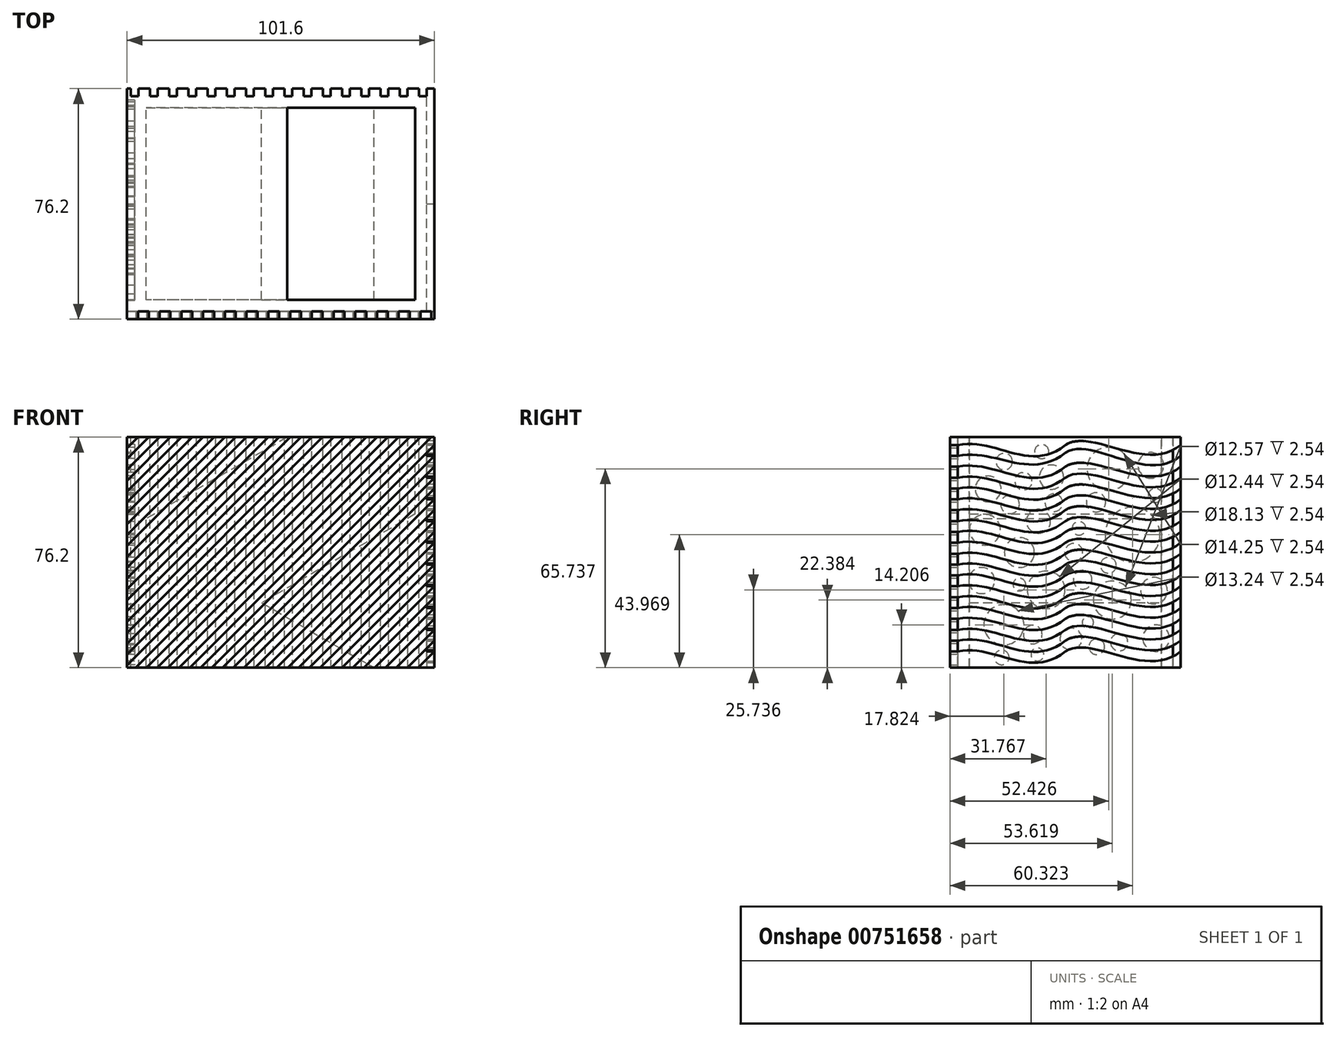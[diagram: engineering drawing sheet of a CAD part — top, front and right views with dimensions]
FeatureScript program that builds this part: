
annotation { "Feature Type Name" : "Feature", "Feature Type Description" : "" }
export const myFeature = defineFeature(function(context is Context, id is Id, definition is map)
    precondition{}
    {
        {
            var Q0;
            Q0=qCreatedBy(makeId("Front.planeOp"),FACE);
            var sketch = newSketch(context, id + "F0", { "sketchPlane" : qUnion([Q0])});
            skLineSegment(sketch, "E0.bottom", {"start": v(50.8, 38.1) * mm, "end": v(-50.8, 38.1) * mm});
            skLineSegment(sketch, "E0.top", {"start": v(50.8, -38.1) * mm, "end": v(-50.8, -38.1) * mm});
            skLineSegment(sketch, "E0.left", {"start": v(50.8, 38.1) * mm, "end": v(50.8, -38.1) * mm});
            skLineSegment(sketch, "E0.right", {"start": v(-50.8, 38.1) * mm, "end": v(-50.8, -38.1) * mm});
            skPoint(sketch, "E0.middle", {"position": v(0, 0) * mm});
            skLineSegment(sketch, "E1", {"start": v(44.45, -38.1) * mm, "end": v(44.45, 38.1) * mm});
            skLineSegment(sketch, "E2.MirrorCS", {"start": v(-44.45, -38.1) * mm, "end": v(-44.45, 38.1) * mm});
            skLineSegment(sketch, "E3", {"start": v(44.45, 12.7) * mm, "end": v(-6.35, -16.63) * mm});
            skLineSegment(sketch, "E4", {"start": v(-6.35, -16.63) * mm, "end": v(30.84, -38.1) * mm});
            skLineSegment(sketch, "E5", {"start": v(2.16, 38.1) * mm, "end": v(-44.45, 11.2) * mm});
            skSolve(sketch);
        }
        {
            var Q0;
            {var subQ0=sQuery(id+"F0.wireOp",EDGE,"E0.left");Q0=makeQuery(id+"F0.imprint","IMPRINT",FACE,{"disambiguationData":[TD([[makeQuery(id+"F0.imprint","IMPRINT",EDGE,{"derivedFrom":subQ0}),-1.0]])]});}
            var Q1;
            {var subQ0=sQuery(id+"F0.wireOp",EDGE,"E0.right");Q1=makeQuery(id+"F0.imprint","IMPRINT",FACE,{"disambiguationData":[TD([[makeQuery(id+"F0.imprint","IMPRINT",EDGE,{"derivedFrom":subQ0}),1.0]])]});}
            var Q2;
            {var subQ4=sQuery(id+"F0.wireOp",EDGE,"E3");Q2=makeQuery(id+"F0.imprint","IMPRINT",FACE,{"disambiguationData":[TD([[makeQuery(id+"F0.imprint","IMPRINT",EDGE,{"derivedFrom":subQ4}),1.0]])]});}
            var Q3;
            {var subQ3=sQuery(id+"F0.wireOp",EDGE,"E5");Q3=makeQuery(id+"F0.imprint","IMPRINT",FACE,{"disambiguationData":[TD([[makeQuery(id+"F0.imprint","IMPRINT",EDGE,{"derivedFrom":subQ3}),-1.0]])]});}
            extrude(context, id + "F1", {"entities" : qUnion([Q0, Q1, Q2, Q3]), "endBound" : BoundingType.SYMMETRIC, "depth" : 76.2 * mm, "offsetDistance" : 25.4 * mm});
        }
        {
            var Q0;
            Q0=makeQuery(id+"F1.opExtrude","CAP_FACE",FACE,{"disambiguationData":[OSD([sQuery(id+"F0.wireOp",EDGE,"E0.bottom"),sQuery(id+"F0.wireOp",EDGE,"E0.top"),sQuery(id+"F0.wireOp",EDGE,"E0.left"),sQuery(id+"F0.wireOp",EDGE,"E1"),sQuery(id+"F0.wireOp",EDGE,"E3"),sQuery(id+"F0.wireOp",EDGE,"E4")])],"isStart":true});
            var sketch = newSketch(context, id + "F2", { "sketchPlane" : qUnion([Q0])});
            skLineSegment(sketch, "E6.bottom", {"start": v(-50.8, 38.1) * mm, "end": v(50.8, 38.1) * mm});
            skLineSegment(sketch, "E6.top", {"start": v(-50.8, -38.1) * mm, "end": v(50.8, -38.1) * mm});
            skLineSegment(sketch, "E6.left", {"start": v(-50.8, 38.1) * mm, "end": v(-50.8, -38.1) * mm});
            skLineSegment(sketch, "E6.right", {"start": v(50.8, 38.1) * mm, "end": v(50.8, -38.1) * mm});
            skPoint(sketch, "E6.middle", {"position": v(0, 0) * mm});
            skSolve(sketch);
        }
        {
            var Q0;
            Q0 = qSketchRegion(id + "F2", true);
            extrude(context, id + "F3", {"entities" : qUnion([Q0]), "operationType" : NewBodyOperationType.ADD, "oppositeDirection" : true, "depth" : 6.35 * mm, "offsetDistance" : 25.4 * mm});
        }
        {
            var Q0;
            Q0=makeQuery(id+"F1.opExtrude","CAP_FACE",FACE,{"disambiguationData":[OSD([sQuery(id+"F0.wireOp",EDGE,"E0.bottom"),sQuery(id+"F0.wireOp",EDGE,"E0.top"),sQuery(id+"F0.wireOp",EDGE,"E0.right"),sQuery(id+"F0.wireOp",EDGE,"E2.MirrorCS"),sQuery(id+"F0.wireOp",EDGE,"E5")])],"isStart":false});
            var sketch = newSketch(context, id + "F4", { "sketchPlane" : qUnion([Q0])});
            skLineSegment(sketch, "E7.bottom", {"start": v(-50.8, 38.1) * mm, "end": v(50.8, 38.1) * mm});
            skLineSegment(sketch, "E7.top", {"start": v(-50.8, -38.1) * mm, "end": v(50.8, -38.1) * mm});
            skLineSegment(sketch, "E7.left", {"start": v(-50.8, 38.1) * mm, "end": v(-50.8, -38.1) * mm});
            skLineSegment(sketch, "E7.right", {"start": v(50.8, 38.1) * mm, "end": v(50.8, -38.1) * mm});
            skPoint(sketch, "E7.middle", {"position": v(0, 0) * mm});
            skSolve(sketch);
        }
        {
            var Q0;
            Q0 = qSketchRegion(id + "F4", true);
            extrude(context, id + "F5", {"entities" : qUnion([Q0]), "operationType" : NewBodyOperationType.ADD, "oppositeDirection" : true, "depth" : 6.35 * mm, "offsetDistance" : 25.4 * mm});
        }
        {
            var Q0;
            {var subQ0=sQuery(id+"F0.wireOp",EDGE,"E0.top");var subQ1=sQuery(id+"F0.wireOp",EDGE,"E0.bottom");Q0=makeQuery(id+"F5.boolean.opBoolean","MERGE",FACE,{"derivedFrom":[makeQuery(id+"F1.opExtrude","CAP_FACE",FACE,{"disambiguationData":[OSD([subQ1,subQ0,sQuery(id+"F0.wireOp",EDGE,"E0.left"),sQuery(id+"F0.wireOp",EDGE,"E1"),sQuery(id+"F0.wireOp",EDGE,"E3"),sQuery(id+"F0.wireOp",EDGE,"E4")])],"isStart":false}),makeQuery(id+"F1.opExtrude","CAP_FACE",FACE,{"disambiguationData":[OSD([subQ1,subQ0,sQuery(id+"F0.wireOp",EDGE,"E0.right"),sQuery(id+"F0.wireOp",EDGE,"E2.MirrorCS"),sQuery(id+"F0.wireOp",EDGE,"E5")])],"isStart":false}),makeQuery(id+"F5.opExtrude","CAP_FACE",FACE,{"disambiguationData":[OSD([sQuery(id+"F4.wireOp",EDGE,"E7.bottom"),sQuery(id+"F4.wireOp",EDGE,"E7.top"),sQuery(id+"F4.wireOp",EDGE,"E7.left"),sQuery(id+"F4.wireOp",EDGE,"E7.right")])],"isStart":true})]});}
            var sketch = newSketch(context, id + "F6", { "sketchPlane" : qUnion([Q0])});
            skLineSegment(sketch, "E8", {"start": v(-50.8, 34.5) * mm, "end": v(-47.2, 38.1) * mm});
            skLineSegment(sketch, "E9", {"start": v(-50.8, 30.92) * mm, "end": v(-43.62, 38.1) * mm});
            skLineSegment(sketch, "E10", {"start": v(-50.8, 27.32) * mm, "end": v(-40.02, 38.1) * mm});
            skLineSegment(sketch, "E11", {"start": v(-50.8, 23.73) * mm, "end": v(-36.43, 38.1) * mm});
            skLineSegment(sketch, "E12", {"start": v(-50.8, 20.14) * mm, "end": v(-32.84, 38.1) * mm});
            skLineSegment(sketch, "E13", {"start": v(-50.8, 16.55) * mm, "end": v(-29.25, 38.1) * mm});
            skLineSegment(sketch, "E14", {"start": v(-50.8, 12.96) * mm, "end": v(-25.66, 38.1) * mm});
            skLineSegment(sketch, "E15", {"start": v(-50.8, 9.36) * mm, "end": v(-22.06, 38.1) * mm});
            skLineSegment(sketch, "E16", {"start": v(-50.8, 5.77) * mm, "end": v(-18.47, 38.1) * mm});
            skLineSegment(sketch, "E17", {"start": v(-50.8, 2.18) * mm, "end": v(-14.88, 38.1) * mm});
            skLineSegment(sketch, "E18", {"start": v(-50.8, -1.41) * mm, "end": v(-11.29, 38.1) * mm});
            skLineSegment(sketch, "E19", {"start": v(-50.8, -5) * mm, "end": v(-7.7, 38.1) * mm});
            skLineSegment(sketch, "E20", {"start": v(-4.1, 38.1) * mm, "end": v(-50.8, -8.6) * mm});
            skLineSegment(sketch, "E21", {"start": v(-50.8, -12.19) * mm, "end": v(-0.51, 38.1) * mm});
            skLineSegment(sketch, "E22", {"start": v(-50.8, -15.78) * mm, "end": v(3.08, 38.1) * mm});
            skLineSegment(sketch, "E23", {"start": v(6.67, 38.1) * mm, "end": v(-50.8, -19.37) * mm});
            skLineSegment(sketch, "E24", {"start": v(-50.8, -22.97) * mm, "end": v(10.27, 38.1) * mm});
            skLineSegment(sketch, "E25", {"start": v(13.86, 38.1) * mm, "end": v(-50.8, -26.56) * mm});
            skLineSegment(sketch, "E26", {"start": v(-50.8, -30.15) * mm, "end": v(17.45, 38.1) * mm});
            skLineSegment(sketch, "E27", {"start": v(-50.8, -33.74) * mm, "end": v(21.04, 38.1) * mm});
            skLineSegment(sketch, "E28", {"start": v(-50.8, -37.33) * mm, "end": v(24.63, 38.1) * mm});
            skLineSegment(sketch, "E29", {"start": v(-47.97, -38.1) * mm, "end": v(28.23, 38.1) * mm});
            skLineSegment(sketch, "E30", {"start": v(-44.38, -38.1) * mm, "end": v(31.82, 38.1) * mm});
            skLineSegment(sketch, "E31", {"start": v(35.41, 38.1) * mm, "end": v(-40.79, -38.1) * mm});
            skLineSegment(sketch, "E32", {"start": v(-37.2, -38.1) * mm, "end": v(39, 38.1) * mm});
            skLineSegment(sketch, "E33", {"start": v(42.6, 38.1) * mm, "end": v(-33.6, -38.1) * mm});
            skLineSegment(sketch, "E34", {"start": v(-30.01, -38.1) * mm, "end": v(46.19, 38.1) * mm});
            skLineSegment(sketch, "E35", {"start": v(49.78, 38.1) * mm, "end": v(-26.42, -38.1) * mm});
            skLineSegment(sketch, "E36", {"start": v(50.8, 35.53) * mm, "end": v(-22.83, -38.1) * mm});
            skLineSegment(sketch, "E37", {"start": v(-19.24, -38.1) * mm, "end": v(50.8, 31.94) * mm});
            skLineSegment(sketch, "E38", {"start": v(50.8, 28.34) * mm, "end": v(-15.64, -38.1) * mm});
            skLineSegment(sketch, "E39", {"start": v(-12.05, -38.1) * mm, "end": v(50.8, 24.75) * mm});
            skLineSegment(sketch, "E40", {"start": v(50.8, 21.16) * mm, "end": v(-8.46, -38.1) * mm});
            skLineSegment(sketch, "E41", {"start": v(-4.87, -38.1) * mm, "end": v(50.8, 17.57) * mm});
            skLineSegment(sketch, "E42", {"start": v(50.8, 13.98) * mm, "end": v(-1.28, -38.1) * mm});
            skLineSegment(sketch, "E43", {"start": v(2.32, -38.1) * mm, "end": v(50.8, 10.38) * mm});
            skLineSegment(sketch, "E44", {"start": v(50.8, 6.8) * mm, "end": v(5.9, -38.1) * mm});
            skLineSegment(sketch, "E45", {"start": v(9.5, -38.1) * mm, "end": v(50.8, 3.2) * mm});
            skLineSegment(sketch, "E46", {"start": v(50.8, -0.4) * mm, "end": v(13.1, -38.1) * mm});
            skLineSegment(sketch, "E47", {"start": v(16.68, -38.1) * mm, "end": v(50.8, -3.98) * mm});
            skLineSegment(sketch, "E48", {"start": v(50.8, -7.58) * mm, "end": v(20.28, -38.1) * mm});
            skLineSegment(sketch, "E49", {"start": v(23.87, -38.1) * mm, "end": v(50.8, -11.17) * mm});
            skLineSegment(sketch, "E50", {"start": v(50.8, -14.76) * mm, "end": v(27.46, -38.1) * mm});
            skLineSegment(sketch, "E51", {"start": v(31.05, -38.1) * mm, "end": v(50.8, -18.35) * mm});
            skLineSegment(sketch, "E52", {"start": v(34.64, -38.1) * mm, "end": v(50.8, -21.94) * mm});
            skLineSegment(sketch, "E53", {"start": v(50.8, -25.54) * mm, "end": v(38.24, -38.1) * mm});
            skLineSegment(sketch, "E54", {"start": v(41.83, -38.1) * mm, "end": v(50.8, -29.13) * mm});
            skLineSegment(sketch, "E55", {"start": v(50.8, -32.72) * mm, "end": v(45.42, -38.1) * mm});
            skLineSegment(sketch, "E56", {"start": v(-47.2, 38.1) * mm, "end": v(-43.62, 38.1) * mm});
            skLineSegment(sketch, "E57", {"start": v(-40.02, 38.1) * mm, "end": v(-36.43, 38.1) * mm});
            skLineSegment(sketch, "E58", {"start": v(-32.84, 38.1) * mm, "end": v(-29.25, 38.1) * mm});
            skLineSegment(sketch, "E59", {"start": v(-25.66, 38.1) * mm, "end": v(-22.06, 38.1) * mm});
            skLineSegment(sketch, "E60", {"start": v(-18.47, 38.1) * mm, "end": v(-14.88, 38.1) * mm});
            skLineSegment(sketch, "E61", {"start": v(-11.29, 38.1) * mm, "end": v(-7.7, 38.1) * mm});
            skLineSegment(sketch, "E62", {"start": v(-4.1, 38.1) * mm, "end": v(-0.51, 38.1) * mm});
            skLineSegment(sketch, "E63", {"start": v(3.08, 38.1) * mm, "end": v(6.67, 38.1) * mm});
            skLineSegment(sketch, "E64", {"start": v(10.27, 38.1) * mm, "end": v(13.86, 38.1) * mm});
            skLineSegment(sketch, "E65", {"start": v(17.45, 38.1) * mm, "end": v(21.04, 38.1) * mm});
            skLineSegment(sketch, "E66", {"start": v(24.63, 38.1) * mm, "end": v(28.23, 38.1) * mm});
            skLineSegment(sketch, "E67", {"start": v(31.82, 38.1) * mm, "end": v(35.41, 38.1) * mm});
            skLineSegment(sketch, "E68", {"start": v(39, 38.1) * mm, "end": v(42.6, 38.1) * mm});
            skLineSegment(sketch, "E69", {"start": v(46.19, 38.1) * mm, "end": v(49.78, 38.1) * mm});
            skLineSegment(sketch, "E70", {"start": v(50.8, 35.53) * mm, "end": v(50.8, 31.94) * mm});
            skLineSegment(sketch, "E71", {"start": v(50.8, 28.34) * mm, "end": v(50.8, 24.75) * mm});
            skLineSegment(sketch, "E72", {"start": v(50.8, 21.16) * mm, "end": v(50.8, 17.57) * mm});
            skLineSegment(sketch, "E73", {"start": v(50.8, 13.98) * mm, "end": v(50.8, 10.38) * mm});
            skLineSegment(sketch, "E74", {"start": v(50.8, 6.8) * mm, "end": v(50.8, 3.2) * mm});
            skLineSegment(sketch, "E75", {"start": v(50.8, -0.4) * mm, "end": v(50.8, -3.98) * mm});
            skLineSegment(sketch, "E76", {"start": v(50.8, -7.58) * mm, "end": v(50.8, -11.17) * mm});
            skLineSegment(sketch, "E77", {"start": v(50.8, -14.76) * mm, "end": v(50.8, -18.35) * mm});
            skLineSegment(sketch, "E78", {"start": v(50.8, -21.94) * mm, "end": v(50.8, -25.54) * mm});
            skLineSegment(sketch, "E79", {"start": v(50.8, -29.13) * mm, "end": v(50.8, -32.72) * mm});
            skLineSegment(sketch, "E80", {"start": v(45.42, -38.1) * mm, "end": v(41.83, -38.1) * mm});
            skLineSegment(sketch, "E81", {"start": v(38.24, -38.1) * mm, "end": v(34.64, -38.1) * mm});
            skLineSegment(sketch, "E82", {"start": v(31.05, -38.1) * mm, "end": v(27.46, -38.1) * mm});
            skLineSegment(sketch, "E83", {"start": v(23.87, -38.1) * mm, "end": v(20.28, -38.1) * mm});
            skLineSegment(sketch, "E84", {"start": v(16.68, -38.1) * mm, "end": v(13.1, -38.1) * mm});
            skLineSegment(sketch, "E85", {"start": v(9.5, -38.1) * mm, "end": v(5.9, -38.1) * mm});
            skLineSegment(sketch, "E86", {"start": v(2.32, -38.1) * mm, "end": v(-1.28, -38.1) * mm});
            skLineSegment(sketch, "E87", {"start": v(-4.87, -38.1) * mm, "end": v(-8.46, -38.1) * mm});
            skLineSegment(sketch, "E88", {"start": v(-12.05, -38.1) * mm, "end": v(-15.64, -38.1) * mm});
            skLineSegment(sketch, "E89", {"start": v(-19.24, -38.1) * mm, "end": v(-22.83, -38.1) * mm});
            skLineSegment(sketch, "E90", {"start": v(-26.42, -38.1) * mm, "end": v(-30.01, -38.1) * mm});
            skLineSegment(sketch, "E91", {"start": v(-33.6, -38.1) * mm, "end": v(-37.2, -38.1) * mm});
            skLineSegment(sketch, "E92", {"start": v(-40.79, -38.1) * mm, "end": v(-44.38, -38.1) * mm});
            skLineSegment(sketch, "E93", {"start": v(-47.97, -38.1) * mm, "end": v(-50.8, -38.1) * mm});
            skLineSegment(sketch, "E94", {"start": v(-50.8, -37.33) * mm, "end": v(-50.8, -38.1) * mm});
            skLineSegment(sketch, "E95", {"start": v(-50.8, -33.74) * mm, "end": v(-50.8, -30.15) * mm});
            skLineSegment(sketch, "E96", {"start": v(-50.8, -26.56) * mm, "end": v(-50.8, -22.97) * mm});
            skLineSegment(sketch, "E97", {"start": v(-50.8, -19.37) * mm, "end": v(-50.8, -15.78) * mm});
            skLineSegment(sketch, "E98", {"start": v(-50.8, -12.19) * mm, "end": v(-50.8, -8.6) * mm});
            skLineSegment(sketch, "E99", {"start": v(-50.8, -5) * mm, "end": v(-50.8, -1.41) * mm});
            skLineSegment(sketch, "E100", {"start": v(-50.8, 2.18) * mm, "end": v(-50.8, 5.77) * mm});
            skLineSegment(sketch, "E101", {"start": v(-50.8, 9.36) * mm, "end": v(-50.8, 12.96) * mm});
            skLineSegment(sketch, "E102", {"start": v(-50.8, 16.55) * mm, "end": v(-50.8, 20.14) * mm});
            skLineSegment(sketch, "E103", {"start": v(-50.8, 23.73) * mm, "end": v(-50.8, 27.32) * mm});
            skLineSegment(sketch, "E104", {"start": v(-50.8, 30.92) * mm, "end": v(-50.8, 34.5) * mm});
            skSolve(sketch);
        }
        {
            var Q0;
            Q0 = qSketchRegion(id + "F6", true);
            extrude(context, id + "F7", {"entities" : qUnion([Q0]), "operationType" : NewBodyOperationType.REMOVE, "oppositeDirection" : true, "depth" : 2.54 * mm, "offsetDistance" : 25.4 * mm});
        }
        {
            var Q0;
            {var subQ0=sQuery(id+"F0.wireOp",EDGE,"E0.top");var subQ1=sQuery(id+"F0.wireOp",EDGE,"E0.bottom");Q0=makeQuery(id+"F3.boolean.opBoolean","MERGE",FACE,{"derivedFrom":[makeQuery(id+"F1.opExtrude","CAP_FACE",FACE,{"disambiguationData":[OSD([subQ1,subQ0,sQuery(id+"F0.wireOp",EDGE,"E0.left"),sQuery(id+"F0.wireOp",EDGE,"E1"),sQuery(id+"F0.wireOp",EDGE,"E3"),sQuery(id+"F0.wireOp",EDGE,"E4")])],"isStart":true}),makeQuery(id+"F1.opExtrude","CAP_FACE",FACE,{"disambiguationData":[OSD([subQ1,subQ0,sQuery(id+"F0.wireOp",EDGE,"E0.right"),sQuery(id+"F0.wireOp",EDGE,"E2.MirrorCS"),sQuery(id+"F0.wireOp",EDGE,"E5")])],"isStart":true}),makeQuery(id+"F3.opExtrude","CAP_FACE",FACE,{"disambiguationData":[OSD([sQuery(id+"F2.wireOp",EDGE,"E6.bottom"),sQuery(id+"F2.wireOp",EDGE,"E6.top"),sQuery(id+"F2.wireOp",EDGE,"E6.left"),sQuery(id+"F2.wireOp",EDGE,"E6.right")])],"isStart":true})]});}
            var sketch = newSketch(context, id + "F8", { "sketchPlane" : qUnion([Q0])});
            skLineSegment(sketch, "E105", {"start": v(-48.26, 38.1) * mm, "end": v(-48.26, -38.1) * mm});
            skLineSegment(sketch, "E106", {"start": v(-48.26, -38.1) * mm, "end": v(-45.72, -38.1) * mm});
            skLineSegment(sketch, "E107", {"start": v(-45.72, -38.1) * mm, "end": v(-45.72, 38.1) * mm});
            skLineSegment(sketch, "E108", {"start": v(-45.72, 38.1) * mm, "end": v(-48.26, 38.1) * mm});
            skLineSegment(sketch, "E109.1.0.0", {"start": v(-39.37, -38.1) * mm, "end": v(-39.37, 38.1) * mm});
            skLineSegment(sketch, "E109.1.0.1", {"start": v(-41.91, 38.1) * mm, "end": v(-41.9, -38.1) * mm});
            skLineSegment(sketch, "E109.1.0.2", {"start": v(-39.37, 38.1) * mm, "end": v(-41.91, 38.1) * mm});
            skLineSegment(sketch, "E109.1.0.3", {"start": v(-41.9, -38.1) * mm, "end": v(-39.37, -38.1) * mm});
            skLineSegment(sketch, "E109.2.0.0", {"start": v(-33.02, -38.1) * mm, "end": v(-33.02, 38.1) * mm});
            skLineSegment(sketch, "E109.2.0.1", {"start": v(-35.56, 38.1) * mm, "end": v(-35.56, -38.1) * mm});
            skLineSegment(sketch, "E109.2.0.2", {"start": v(-33.02, 38.1) * mm, "end": v(-35.56, 38.1) * mm});
            skLineSegment(sketch, "E109.2.0.3", {"start": v(-35.56, -38.1) * mm, "end": v(-33.02, -38.1) * mm});
            skLineSegment(sketch, "E109.3.0.0", {"start": v(-26.67, -38.1) * mm, "end": v(-26.67, 38.1) * mm});
            skLineSegment(sketch, "E109.3.0.1", {"start": v(-29.2, 38.1) * mm, "end": v(-29.2, -38.1) * mm});
            skLineSegment(sketch, "E109.3.0.2", {"start": v(-26.67, 38.1) * mm, "end": v(-29.21, 38.1) * mm});
            skLineSegment(sketch, "E109.3.0.3", {"start": v(-29.2, -38.1) * mm, "end": v(-26.67, -38.1) * mm});
            skLineSegment(sketch, "E109.4.0.0", {"start": v(-20.32, -38.1) * mm, "end": v(-20.32, 38.1) * mm});
            skLineSegment(sketch, "E109.4.0.1", {"start": v(-22.86, 38.1) * mm, "end": v(-22.86, -38.1) * mm});
            skLineSegment(sketch, "E109.4.0.2", {"start": v(-20.32, 38.1) * mm, "end": v(-22.86, 38.1) * mm});
            skLineSegment(sketch, "E109.4.0.3", {"start": v(-22.86, -38.1) * mm, "end": v(-20.32, -38.1) * mm});
            skLineSegment(sketch, "E109.5.0.0", {"start": v(-13.97, -38.1) * mm, "end": v(-13.97, 38.1) * mm});
            skLineSegment(sketch, "E109.5.0.1", {"start": v(-16.5, 38.1) * mm, "end": v(-16.5, -38.1) * mm});
            skLineSegment(sketch, "E109.5.0.2", {"start": v(-13.97, 38.1) * mm, "end": v(-16.5, 38.1) * mm});
            skLineSegment(sketch, "E109.5.0.3", {"start": v(-16.5, -38.1) * mm, "end": v(-13.97, -38.1) * mm});
            skLineSegment(sketch, "E109.6.0.0", {"start": v(-7.62, -38.1) * mm, "end": v(-7.62, 38.1) * mm});
            skLineSegment(sketch, "E109.6.0.1", {"start": v(-10.16, 38.1) * mm, "end": v(-10.16, -38.1) * mm});
            skLineSegment(sketch, "E109.6.0.2", {"start": v(-7.62, 38.1) * mm, "end": v(-10.16, 38.1) * mm});
            skLineSegment(sketch, "E109.6.0.3", {"start": v(-10.16, -38.1) * mm, "end": v(-7.62, -38.1) * mm});
            skLineSegment(sketch, "E109.7.0.0", {"start": v(-1.27, -38.1) * mm, "end": v(-1.27, 38.1) * mm});
            skLineSegment(sketch, "E109.7.0.1", {"start": v(-3.8, 38.1) * mm, "end": v(-3.8, -38.1) * mm});
            skLineSegment(sketch, "E109.7.0.2", {"start": v(-1.27, 38.1) * mm, "end": v(-3.8, 38.1) * mm});
            skLineSegment(sketch, "E109.7.0.3", {"start": v(-3.8, -38.1) * mm, "end": v(-1.27, -38.1) * mm});
            skLineSegment(sketch, "E109.8.0.0", {"start": v(5.08, -38.1) * mm, "end": v(5.08, 38.1) * mm});
            skLineSegment(sketch, "E109.8.0.1", {"start": v(2.54, 38.1) * mm, "end": v(2.54, -38.1) * mm});
            skLineSegment(sketch, "E109.8.0.2", {"start": v(5.08, 38.1) * mm, "end": v(2.54, 38.1) * mm});
            skLineSegment(sketch, "E109.8.0.3", {"start": v(2.54, -38.1) * mm, "end": v(5.08, -38.1) * mm});
            skLineSegment(sketch, "E109.9.0.0", {"start": v(11.43, -38.1) * mm, "end": v(11.43, 38.1) * mm});
            skLineSegment(sketch, "E109.9.0.1", {"start": v(8.9, 38.1) * mm, "end": v(8.9, -38.1) * mm});
            skLineSegment(sketch, "E109.9.0.2", {"start": v(11.43, 38.1) * mm, "end": v(8.9, 38.1) * mm});
            skLineSegment(sketch, "E109.9.0.3", {"start": v(8.9, -38.1) * mm, "end": v(11.43, -38.1) * mm});
            skLineSegment(sketch, "E109.10.0.0", {"start": v(17.78, -38.1) * mm, "end": v(17.78, 38.1) * mm});
            skLineSegment(sketch, "E109.10.0.1", {"start": v(15.24, 38.1) * mm, "end": v(15.24, -38.1) * mm});
            skLineSegment(sketch, "E109.10.0.2", {"start": v(17.78, 38.1) * mm, "end": v(15.24, 38.1) * mm});
            skLineSegment(sketch, "E109.10.0.3", {"start": v(15.24, -38.1) * mm, "end": v(17.78, -38.1) * mm});
            skLineSegment(sketch, "E109.11.0.0", {"start": v(24.13, -38.1) * mm, "end": v(24.13, 38.1) * mm});
            skLineSegment(sketch, "E109.11.0.1", {"start": v(21.6, 38.1) * mm, "end": v(21.6, -38.1) * mm});
            skLineSegment(sketch, "E109.11.0.2", {"start": v(24.13, 38.1) * mm, "end": v(21.6, 38.1) * mm});
            skLineSegment(sketch, "E109.11.0.3", {"start": v(21.6, -38.1) * mm, "end": v(24.13, -38.1) * mm});
            skLineSegment(sketch, "E109.12.0.0", {"start": v(30.48, -38.1) * mm, "end": v(30.48, 38.1) * mm});
            skLineSegment(sketch, "E109.12.0.1", {"start": v(27.94, 38.1) * mm, "end": v(27.94, -38.1) * mm});
            skLineSegment(sketch, "E109.12.0.2", {"start": v(30.48, 38.1) * mm, "end": v(27.94, 38.1) * mm});
            skLineSegment(sketch, "E109.12.0.3", {"start": v(27.94, -38.1) * mm, "end": v(30.48, -38.1) * mm});
            skLineSegment(sketch, "E109.13.0.0", {"start": v(36.83, -38.1) * mm, "end": v(36.83, 38.1) * mm});
            skLineSegment(sketch, "E109.13.0.1", {"start": v(34.3, 38.1) * mm, "end": v(34.3, -38.1) * mm});
            skLineSegment(sketch, "E109.13.0.2", {"start": v(36.83, 38.1) * mm, "end": v(34.3, 38.1) * mm});
            skLineSegment(sketch, "E109.13.0.3", {"start": v(34.3, -38.1) * mm, "end": v(36.83, -38.1) * mm});
            skLineSegment(sketch, "E109.14.0.0", {"start": v(43.18, -38.1) * mm, "end": v(43.18, 38.1) * mm});
            skLineSegment(sketch, "E109.14.0.1", {"start": v(40.64, 38.1) * mm, "end": v(40.64, -38.1) * mm});
            skLineSegment(sketch, "E109.14.0.2", {"start": v(43.18, 38.1) * mm, "end": v(40.64, 38.1) * mm});
            skLineSegment(sketch, "E109.14.0.3", {"start": v(40.64, -38.1) * mm, "end": v(43.18, -38.1) * mm});
            skLineSegment(sketch, "E109.15.0.0", {"start": v(49.53, -38.1) * mm, "end": v(49.53, 38.1) * mm});
            skLineSegment(sketch, "E109.15.0.1", {"start": v(47, 38.1) * mm, "end": v(47, -38.1) * mm});
            skLineSegment(sketch, "E109.15.0.2", {"start": v(49.53, 38.1) * mm, "end": v(47, 38.1) * mm});
            skLineSegment(sketch, "E109.15.0.3", {"start": v(47, -38.1) * mm, "end": v(49.53, -38.1) * mm});
            skLineSegment(sketch, "E109.direction1", {"start": v(-48.26, -38.1) * mm, "end": v(-41.9, -38.1) * mm, "construction": true});
            skLineSegment(sketch, "E109.direction2", {"start": v(-48.26, -38.1) * mm, "end": v(-48.26, -38.1) * mm});
            skSolve(sketch);
        }
        {
            var Q0;
            Q0 = qSketchRegion(id + "F8", true);
            extrude(context, id + "F9", {"entities" : qUnion([Q0]), "operationType" : NewBodyOperationType.REMOVE, "oppositeDirection" : true, "depth" : 2.54 * mm, "offsetDistance" : 25.4 * mm});
        }
        {
            var Q0;
            Q0=makeQuery(id+"F1.opExtrude","SWEPT_FACE",FACE,{"disambiguationData":[OSD([sQuery(id+"F0.wireOp",EDGE,"E0.left")])]});
            var sketch = newSketch(context, id + "F10", { "sketchPlane" : qUnion([Q0])});
            skFitSpline(sketch, "E110", {"points": [v(-35.56, 35.53) * mm, v(0, 35.53) * mm], "startDerivative": vector(37.13, 7.71) * mm, "endDerivative": vector(34.71, 28.52) * mm});
            skFitSpline(sketch, "E111", {"points": [v(0, 35.53) * mm, v(38.1, 35.53) * mm], "startDerivative": vector(26.16, 17.14) * mm, "endDerivative": vector(34.71, 28.52) * mm});
            skFitSpline(sketch, "E112", {"points": [v(-35.56, 31.94) * mm, v(0, 32.99) * mm], "startDerivative": vector(37.13, 7.71) * mm, "endDerivative": vector(34.71, 28.52) * mm});
            skFitSpline(sketch, "E113", {"points": [v(0, 32.99) * mm, v(38.1, 31.94) * mm], "startDerivative": vector(26.16, 17.14) * mm, "endDerivative": vector(34.71, 28.52) * mm});
            skLineSegment(sketch, "E114", {"start": v(-35.56, 31.94) * mm, "end": v(-35.56, 35.53) * mm});
            skLineSegment(sketch, "E115", {"start": v(38.1, 31.94) * mm, "end": v(38.1, 35.53) * mm});
            skFitSpline(sketch, "E116", {"points": [v(-35.56, 28.34) * mm, v(0, 28.34) * mm], "startDerivative": vector(37.13, 7.71) * mm, "endDerivative": vector(34.71, 28.52) * mm});
            skFitSpline(sketch, "E117", {"points": [v(0, 28.34) * mm, v(38.1, 28.34) * mm], "startDerivative": vector(26.16, 17.14) * mm, "endDerivative": vector(34.71, 28.52) * mm});
            skFitSpline(sketch, "E118", {"points": [v(-35.56, 24.75) * mm, v(0, 24.75) * mm], "startDerivative": vector(37.13, 7.71) * mm, "endDerivative": vector(34.71, 28.52) * mm});
            skFitSpline(sketch, "E119", {"points": [v(0, 24.75) * mm, v(38.1, 24.75) * mm], "startDerivative": vector(26.16, 17.14) * mm, "endDerivative": vector(34.71, 28.52) * mm});
            skLineSegment(sketch, "E120", {"start": v(-35.56, 24.75) * mm, "end": v(-35.56, 28.34) * mm});
            skLineSegment(sketch, "E121", {"start": v(38.1, 28.34) * mm, "end": v(38.1, 24.75) * mm});
            skFitSpline(sketch, "E122", {"points": [v(-35.56, 21.16) * mm, v(0, 21.16) * mm], "startDerivative": vector(37.13, 7.71) * mm, "endDerivative": vector(34.71, 28.52) * mm});
            skFitSpline(sketch, "E123", {"points": [v(0, 21.16) * mm, v(38.1, 21.16) * mm], "startDerivative": vector(26.16, 17.14) * mm, "endDerivative": vector(34.71, 28.52) * mm});
            skFitSpline(sketch, "E124", {"points": [v(-35.56, 17.57) * mm, v(0, 17.57) * mm], "startDerivative": vector(37.13, 7.71) * mm, "endDerivative": vector(34.71, 28.52) * mm});
            skFitSpline(sketch, "E125", {"points": [v(0, 17.57) * mm, v(38.1, 17.57) * mm], "startDerivative": vector(26.16, 17.14) * mm, "endDerivative": vector(34.71, 28.52) * mm});
            skLineSegment(sketch, "E126", {"start": v(-35.56, 17.57) * mm, "end": v(-35.56, 21.16) * mm});
            skLineSegment(sketch, "E127", {"start": v(38.1, 21.16) * mm, "end": v(38.1, 17.57) * mm});
            skFitSpline(sketch, "E128", {"points": [v(-35.56, 13.98) * mm, v(0, 13.98) * mm], "startDerivative": vector(37.13, 7.71) * mm, "endDerivative": vector(34.71, 28.52) * mm});
            skFitSpline(sketch, "E129", {"points": [v(0, 13.98) * mm, v(38.1, 13.98) * mm], "startDerivative": vector(26.16, 17.14) * mm, "endDerivative": vector(34.71, 28.52) * mm});
            skFitSpline(sketch, "E130", {"points": [v(-35.56, 10.38) * mm, v(0, 10.38) * mm], "startDerivative": vector(37.13, 7.71) * mm, "endDerivative": vector(34.71, 28.52) * mm});
            skFitSpline(sketch, "E131", {"points": [v(0, 10.38) * mm, v(38.1, 10.38) * mm], "startDerivative": vector(26.16, 17.14) * mm, "endDerivative": vector(34.71, 28.52) * mm});
            skLineSegment(sketch, "E132", {"start": v(-35.56, 10.38) * mm, "end": v(-35.56, 13.98) * mm});
            skLineSegment(sketch, "E133", {"start": v(38.1, 13.98) * mm, "end": v(38.1, 10.38) * mm});
            skFitSpline(sketch, "E134", {"points": [v(-35.56, 6.8) * mm, v(0, 6.8) * mm], "startDerivative": vector(37.13, 7.71) * mm, "endDerivative": vector(34.71, 28.52) * mm});
            skFitSpline(sketch, "E135", {"points": [v(0, 6.8) * mm, v(38.1, 6.8) * mm], "startDerivative": vector(26.16, 17.14) * mm, "endDerivative": vector(34.71, 28.52) * mm});
            skFitSpline(sketch, "E136", {"points": [v(-35.56, 3.2) * mm, v(0, 3.2) * mm], "startDerivative": vector(37.13, 7.71) * mm, "endDerivative": vector(34.71, 28.52) * mm});
            skFitSpline(sketch, "E137", {"points": [v(0, 3.2) * mm, v(38.1, 3.2) * mm], "startDerivative": vector(26.16, 17.14) * mm, "endDerivative": vector(34.71, 28.52) * mm});
            skLineSegment(sketch, "E138", {"start": v(-35.56, 3.2) * mm, "end": v(-35.56, 6.8) * mm});
            skLineSegment(sketch, "E139", {"start": v(38.1, 6.8) * mm, "end": v(38.1, 3.2) * mm});
            skFitSpline(sketch, "E140", {"points": [v(-35.56, -0.4) * mm, v(0, -0.4) * mm], "startDerivative": vector(37.13, 7.71) * mm, "endDerivative": vector(34.71, 28.52) * mm});
            skFitSpline(sketch, "E141", {"points": [v(0, -0.4) * mm, v(38.1, -0.4) * mm], "startDerivative": vector(26.16, 17.14) * mm, "endDerivative": vector(34.71, 28.52) * mm});
            skFitSpline(sketch, "E142", {"points": [v(-35.56, -3.98) * mm, v(0, -3.98) * mm], "startDerivative": vector(37.13, 7.71) * mm, "endDerivative": vector(34.71, 28.52) * mm});
            skFitSpline(sketch, "E143", {"points": [v(0, -3.98) * mm, v(38.1, -3.98) * mm], "startDerivative": vector(26.16, 17.14) * mm, "endDerivative": vector(34.71, 28.52) * mm});
            skLineSegment(sketch, "E144", {"start": v(-35.56, -3.98) * mm, "end": v(-35.56, -0.4) * mm});
            skLineSegment(sketch, "E145", {"start": v(38.1, -0.4) * mm, "end": v(38.1, -3.98) * mm});
            skFitSpline(sketch, "E146", {"points": [v(-35.56, -7.58) * mm, v(0, -7.58) * mm], "startDerivative": vector(37.13, 7.71) * mm, "endDerivative": vector(34.71, 28.52) * mm});
            skFitSpline(sketch, "E147", {"points": [v(0, -7.58) * mm, v(38.1, -7.58) * mm], "startDerivative": vector(26.16, 17.14) * mm, "endDerivative": vector(34.71, 28.52) * mm});
            skFitSpline(sketch, "E148", {"points": [v(-35.56, -11.17) * mm, v(0, -11.17) * mm], "startDerivative": vector(37.13, 7.71) * mm, "endDerivative": vector(34.71, 28.52) * mm});
            skFitSpline(sketch, "E149", {"points": [v(0, -11.17) * mm, v(38.1, -11.17) * mm], "startDerivative": vector(26.16, 17.14) * mm, "endDerivative": vector(34.71, 28.52) * mm});
            skLineSegment(sketch, "E150", {"start": v(-35.56, -11.17) * mm, "end": v(-35.56, -7.58) * mm});
            skLineSegment(sketch, "E151", {"start": v(38.1, -7.58) * mm, "end": v(38.1, -11.17) * mm});
            skFitSpline(sketch, "E152", {"points": [v(-35.56, -14.76) * mm, v(0, -14.76) * mm], "startDerivative": vector(37.13, 7.71) * mm, "endDerivative": vector(34.71, 28.52) * mm});
            skFitSpline(sketch, "E153", {"points": [v(0, -14.76) * mm, v(38.1, -14.76) * mm], "startDerivative": vector(26.16, 17.14) * mm, "endDerivative": vector(34.71, 28.52) * mm});
            skFitSpline(sketch, "E154", {"points": [v(-35.56, -18.35) * mm, v(0, -18.35) * mm], "startDerivative": vector(37.13, 7.71) * mm, "endDerivative": vector(34.71, 28.52) * mm});
            skFitSpline(sketch, "E155", {"points": [v(0, -18.35) * mm, v(38.1, -18.35) * mm], "startDerivative": vector(26.16, 17.14) * mm, "endDerivative": vector(34.71, 28.52) * mm});
            skLineSegment(sketch, "E156", {"start": v(-35.56, -18.35) * mm, "end": v(-35.56, -14.76) * mm});
            skLineSegment(sketch, "E157", {"start": v(38.1, -14.76) * mm, "end": v(38.1, -18.35) * mm});
            skFitSpline(sketch, "E158", {"points": [v(-35.56, -21.94) * mm, v(0, -21.94) * mm], "startDerivative": vector(37.13, 7.71) * mm, "endDerivative": vector(34.71, 28.52) * mm});
            skFitSpline(sketch, "E159", {"points": [v(0, -21.94) * mm, v(38.1, -21.94) * mm], "startDerivative": vector(26.16, 17.14) * mm, "endDerivative": vector(34.71, 28.52) * mm});
            skFitSpline(sketch, "E160", {"points": [v(-35.56, -25.54) * mm, v(0, -25.54) * mm], "startDerivative": vector(37.13, 7.71) * mm, "endDerivative": vector(34.71, 28.52) * mm});
            skFitSpline(sketch, "E161", {"points": [v(0, -25.54) * mm, v(38.1, -25.54) * mm], "startDerivative": vector(26.16, 17.14) * mm, "endDerivative": vector(34.71, 28.52) * mm});
            skLineSegment(sketch, "E162", {"start": v(-35.56, -25.54) * mm, "end": v(-35.56, -21.94) * mm});
            skLineSegment(sketch, "E163", {"start": v(38.1, -21.94) * mm, "end": v(38.1, -25.54) * mm});
            skFitSpline(sketch, "E164", {"points": [v(-35.56, -29.13) * mm, v(0, -29.13) * mm], "startDerivative": vector(37.13, 7.71) * mm, "endDerivative": vector(34.71, 28.52) * mm});
            skFitSpline(sketch, "E165", {"points": [v(0, -29.13) * mm, v(38.1, -29.13) * mm], "startDerivative": vector(26.16, 17.14) * mm, "endDerivative": vector(34.71, 28.52) * mm});
            skFitSpline(sketch, "E166", {"points": [v(-35.56, -32.72) * mm, v(0, -32.72) * mm], "startDerivative": vector(37.13, 7.71) * mm, "endDerivative": vector(34.71, 28.52) * mm});
            skFitSpline(sketch, "E167", {"points": [v(0, -32.72) * mm, v(38.1, -32.72) * mm], "startDerivative": vector(26.16, 17.14) * mm, "endDerivative": vector(34.71, 28.52) * mm});
            skLineSegment(sketch, "E168", {"start": v(-35.56, -32.72) * mm, "end": v(-35.56, -29.13) * mm});
            skLineSegment(sketch, "E169", {"start": v(38.1, -29.13) * mm, "end": v(38.1, -32.72) * mm});
            skSolve(sketch);
        }
        {
            var Q0;
            Q0 = qSketchRegion(id + "F10", true);
            extrude(context, id + "F11", {"entities" : qUnion([Q0]), "operationType" : NewBodyOperationType.REMOVE, "oppositeDirection" : true, "depth" : 2.54 * mm, "offsetDistance" : 25.4 * mm});
        }
        {
            var Q0;
            Q0=makeQuery(id+"F1.opExtrude","SWEPT_FACE",FACE,{"disambiguationData":[OSD([sQuery(id+"F0.wireOp",EDGE,"E0.right")])]});
            var sketch = newSketch(context, id + "F12", { "sketchPlane" : qUnion([Q0])});
            skCircle(sketch, "E170", {"center": v(-28.26, 28.8) * mm, "radius": 4.28 * mm});
            skCircle(sketch, "E171", {"center": v(-14.33, 27.64) * mm, "radius": 7.13 * mm});
            skCircle(sketch, "E172", {"center": v(-22.22, 5.87) * mm, "radius": 9.07 * mm});
            skCircle(sketch, "E173", {"center": v(-4.53, 8.01) * mm, "radius": 2.23 * mm});
            skCircle(sketch, "E174", {"center": v(-2.78, 0) * mm, "radius": 2.97 * mm});
            skCircle(sketch, "E175", {"center": v(-15.52, -15.72) * mm, "radius": 6.28 * mm});
            skCircle(sketch, "E176", {"center": v(6.33, -12.36) * mm, "radius": 6.22 * mm});
            skCircle(sketch, "E177", {"center": v(-1.84, -28.59) * mm, "radius": 3.6 * mm});
            skCircle(sketch, "E178", {"center": v(4.6, 24.9) * mm, "radius": 4.02 * mm});
            skCircle(sketch, "E179", {"center": v(20.18, 30.04) * mm, "radius": 2.72 * mm});
            skCircle(sketch, "E180", {"center": v(18.27, 15.92) * mm, "radius": 3.1 * mm});
            skCircle(sketch, "E181", {"center": v(15.18, 0) * mm, "radius": 4.95 * mm});
            skCircle(sketch, "E182", {"center": v(8.88, 10.3) * mm, "radius": 3.96 * mm});
            skCircle(sketch, "E183", {"center": v(15.18, -10.62) * mm, "radius": 2.1 * mm});
            skCircle(sketch, "E184", {"center": v(20.28, -23.9) * mm, "radius": 6.62 * mm});
            skCircle(sketch, "E185", {"center": v(10.76, -27.11) * mm, "radius": 3.09 * mm});
            skCircle(sketch, "E186", {"center": v(-5.73, -9.01) * mm, "radius": 3.09 * mm});
            skCircle(sketch, "E187", {"center": v(-30, -28.32) * mm, "radius": 4.38 * mm});
            skCircle(sketch, "E188", {"center": v(-10.4, -31.17) * mm, "radius": 2.58 * mm});
            skCircle(sketch, "E189", {"center": v(-17.8, -29.66) * mm, "radius": 2.85 * mm});
            skCircle(sketch, "E190", {"center": v(-7.48, -23.09) * mm, "radius": 1.87 * mm});
            skCircle(sketch, "E191", {"center": v(-29.33, -12.63) * mm, "radius": 4.4 * mm});
            skCircle(sketch, "E192", {"center": v(-29.73, 18.87) * mm, "radius": 2.33 * mm});
            skCircle(sketch, "E193", {"center": v(-10.16, 16.6) * mm, "radius": 3.18 * mm});
            skCircle(sketch, "E194", {"center": v(3.79, 16.46) * mm, "radius": 2.93 * mm});
            skCircle(sketch, "E195", {"center": v(7.8, 33.35) * mm, "radius": 2.34 * mm});
            skCircle(sketch, "E196", {"center": v(13.84, 23.57) * mm, "radius": 2.85 * mm});
            skCircle(sketch, "E197", {"center": v(25.5, 21.02) * mm, "radius": 4.26 * mm});
            skCircle(sketch, "E198", {"center": v(26.58, 7.48) * mm, "radius": 5.09 * mm});
            skCircle(sketch, "E199", {"center": v(27.65, -9.28) * mm, "radius": 4.28 * mm});
            skCircle(sketch, "E200", {"center": v(-14.22, -4.23) * mm, "radius": 2.61 * mm});
            skCircle(sketch, "E201", {"center": v(9.22, -33.73) * mm, "radius": 2.14 * mm});
            skCircle(sketch, "E202", {"center": v(21.02, -34.68) * mm, "radius": 2.43 * mm});
            skSolve(sketch);
        }
        {
            var Q0;
            Q0 = qSketchRegion(id + "F12", true);
            extrude(context, id + "F13", {"entities" : qUnion([Q0]), "operationType" : NewBodyOperationType.REMOVE, "oppositeDirection" : true, "depth" : 2.54 * mm, "offsetDistance" : 25.4 * mm});
        }
    });
